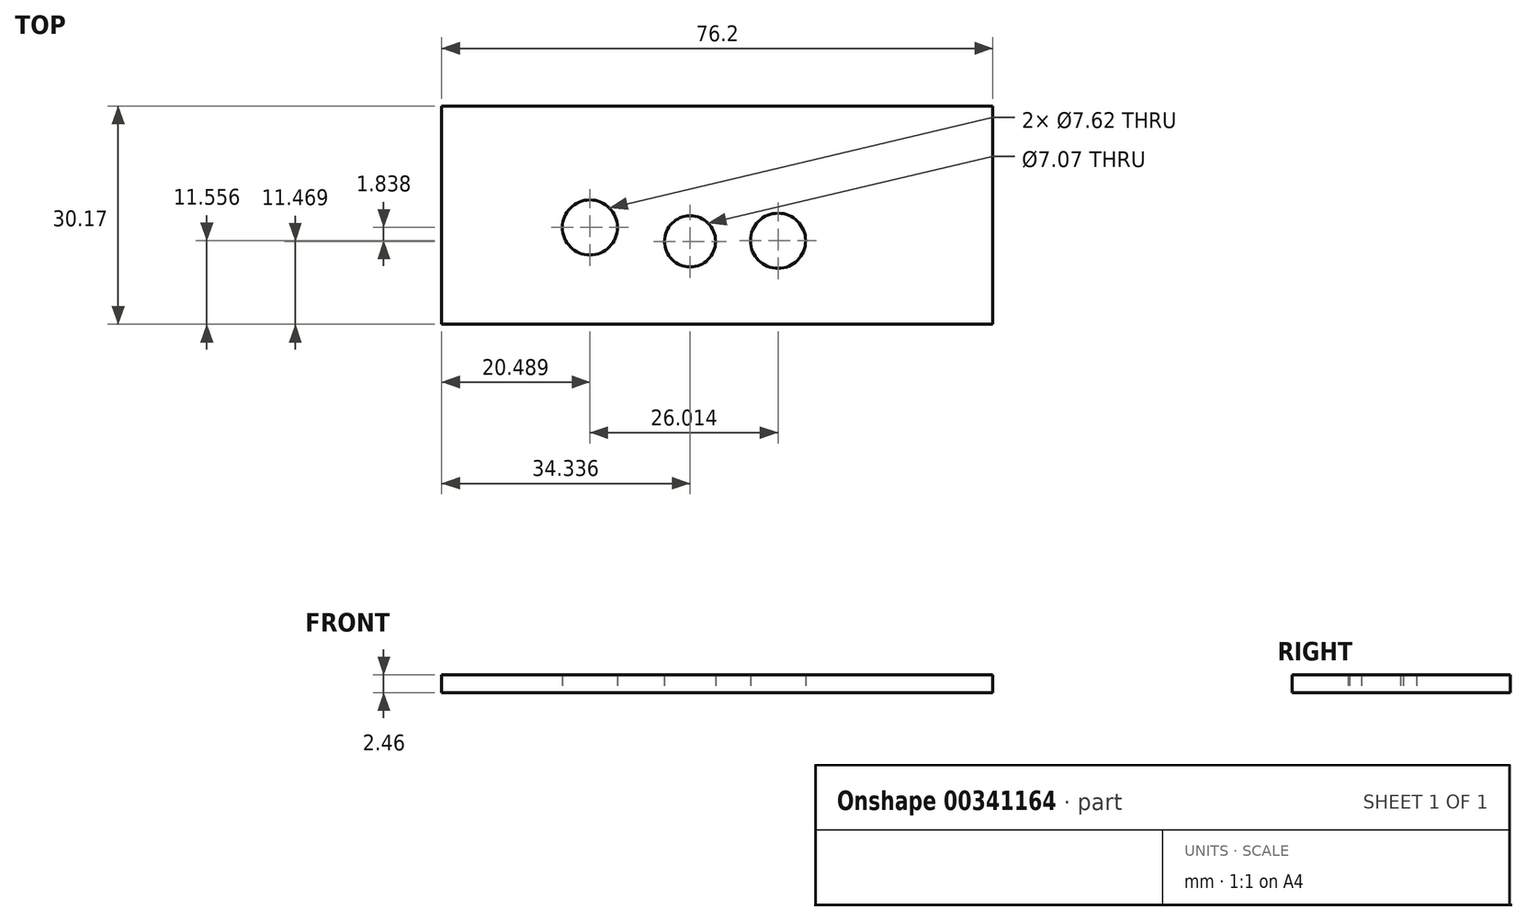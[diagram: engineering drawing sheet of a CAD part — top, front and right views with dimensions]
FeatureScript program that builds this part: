
annotation { "Feature Type Name" : "Feature", "Feature Type Description" : "" }
export const myFeature = defineFeature(function(context is Context, id is Id, definition is map)
    precondition{}
    {
        {
            var Q0;
            Q0=qCreatedBy(makeId("Top.planeOp"),FACE);
            var sketch = newSketch(context, id + "F0", { "sketchPlane" : qUnion([Q0])});
            skLineSegment(sketch, "E0.bottom", {"start": v(-42.93, -28.56) * mm, "end": v(33.27, -28.56) * mm});
            skLineSegment(sketch, "E0.top", {"start": v(-42.93, -58.73) * mm, "end": v(33.27, -58.73) * mm});
            skLineSegment(sketch, "E0.left", {"start": v(-42.93, -28.56) * mm, "end": v(-42.93, -58.73) * mm});
            skLineSegment(sketch, "E0.right", {"start": v(33.27, -28.56) * mm, "end": v(33.27, -58.73) * mm});
            skSolve(sketch);
        }
        {
            var Q0;
            Q0 = qSketchRegion(id + "F0", true);
            extrude(context, id + "F1", {"entities" : qUnion([Q0]), "depth" : 2.46 * mm});
        }
        {
            var Q0;
            Q0=qCreatedBy(makeId("Top.planeOp"),FACE);
            var sketch = newSketch(context, id + "F2", { "sketchPlane" : qUnion([Q0])});
            skCircle(sketch, "E1", {"center": v(-22.44, -45.34) * mm, "radius": 3.81 * mm});
            skCircle(sketch, "E2", {"center": v(-8.6, -47.26) * mm, "radius": 3.54 * mm});
            skCircle(sketch, "E3", {"center": v(3.57, -47.17) * mm, "radius": 3.81 * mm});
            skLineSegment(sketch, "E4", {"start": v(-8.6, -27.05) * mm, "end": v(-8.6, -57.4) * mm});
            skSolve(sketch);
        }
        {
            var Q0;
            Q0 = qSketchRegion(id + "F2", true);
            extrude(context, id + "F3", {"entities" : qUnion([Q0]), "operationType" : NewBodyOperationType.REMOVE, "depth" : 20.32 * mm});
        }
    });
